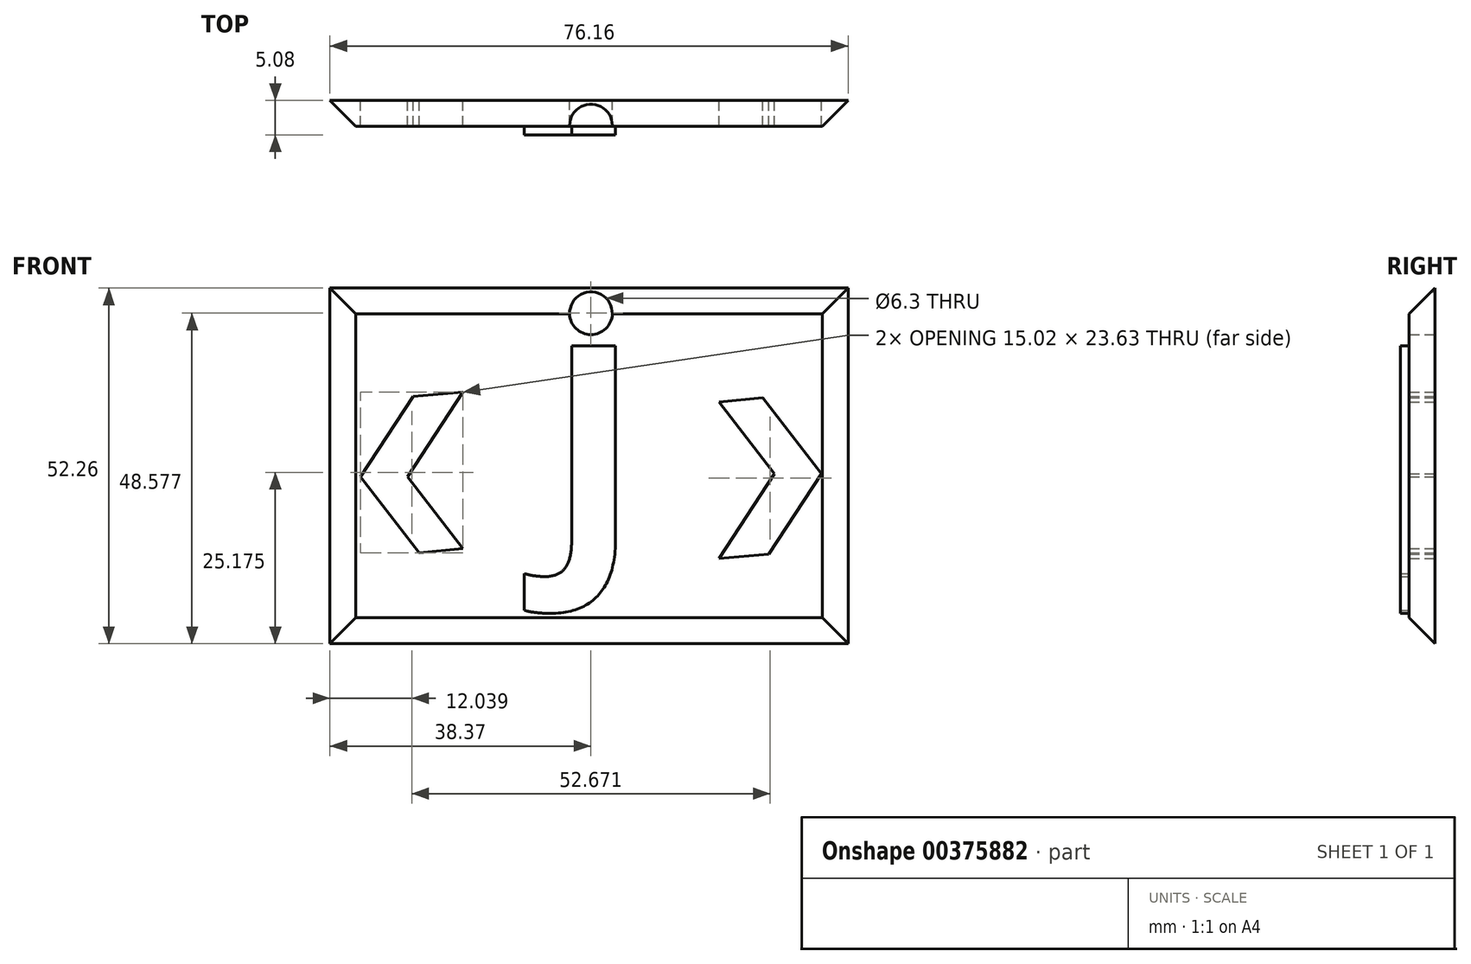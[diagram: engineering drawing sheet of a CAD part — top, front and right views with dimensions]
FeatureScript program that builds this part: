
annotation { "Feature Type Name" : "Feature", "Feature Type Description" : "" }
export const myFeature = defineFeature(function(context is Context, id is Id, definition is map)
    precondition{}
    {
        {
            var Q0;
            Q0=qCreatedBy(makeId("Front.planeOp"),FACE);
            var sketch = newSketch(context, id + "F0", { "sketchPlane" : qUnion([Q0])});
            skPoint(sketch, "E0.cCircle.center.orphan", {"position": v(0, 0) * mm});
            skCircle(sketch, "E1", {"center": v(0, 24.05) * mm, "radius": 3.15 * mm});
            skLineSegment(sketch, "E2", {"start": v(-33.84, 0) * mm, "end": v(-25.23, -11.17) * mm});
            skLineSegment(sketch, "E3", {"start": v(-18.82, 12.46) * mm, "end": v(-26.94, 0) * mm});
            skLineSegment(sketch, "E4", {"start": v(-26.94, 0) * mm, "end": v(-18.82, -10.55) * mm});
            skLineSegment(sketch, "E5", {"start": v(-18.82, -10.55) * mm, "end": v(-25.23, -11.17) * mm});
            skLineSegment(sketch, "E6", {"start": v(-33.84, 0) * mm, "end": v(-26.14, 11.81) * mm});
            skLineSegment(sketch, "E7", {"start": v(-26.14, 11.81) * mm, "end": v(-18.82, 12.46) * mm});
            skText(sketch, "E8", { "text": "J", "fontName": "OpenSans-Bold.ttf"});
            skLineSegment(sketch, "E9", {"start": v(33.85, 0.46) * mm, "end": v(25.24, 11.62) * mm});
            skLineSegment(sketch, "E10", {"start": v(18.83, -12) * mm, "end": v(26.95, 0.46) * mm});
            skLineSegment(sketch, "E11", {"start": v(26.95, 0.46) * mm, "end": v(18.83, 11) * mm});
            skLineSegment(sketch, "E12", {"start": v(18.83, 11) * mm, "end": v(25.24, 11.62) * mm});
            skLineSegment(sketch, "E13", {"start": v(33.85, 0.46) * mm, "end": v(26.15, -11.36) * mm});
            skLineSegment(sketch, "E14", {"start": v(26.15, -11.36) * mm, "end": v(18.83, -12) * mm});
            skLineSegment(sketch, "E15.bottom", {"start": v(39.06, 29) * mm, "end": v(-39.64, 29) * mm});
            skLineSegment(sketch, "E15.top", {"start": v(39.06, -25.8) * mm, "end": v(-39.64, -25.8) * mm});
            skLineSegment(sketch, "E15.left", {"start": v(39.06, 29) * mm, "end": v(39.06, -25.8) * mm});
            skLineSegment(sketch, "E15.right", {"start": v(-39.64, 29) * mm, "end": v(-39.64, -25.8) * mm});
            const initialGuessF0  = {"E8": [-0.00665, -0.01113, 1, 0, 0.03063]};
            skSetInitialGuess(sketch, initialGuessF0);
            skSolve(sketch);
        }
        {
            var Q0;
            Q0=makeQuery(id+"F0.imprint","IMPRINT",FACE,{"disambiguationData":[TD([[makeQuery(id+"F0.imprint","IMPRINT",EDGE,{"derivedFrom":sQuery(id+"F0.wireOp",EDGE,"E1")}),-1.0]])]});
            extrude(context, id + "F1", {"entities" : qUnion([Q0]), "depth" : 3.8 * mm});
        }
        {
            var Q0;
            Q0=makeQuery(id+"F0.imprint","IMPRINT",FACE,{"disambiguationData":[TD([[makeQuery(id+"F0.imprint","IMPRINT",EDGE,{"derivedFrom":sQuery(id+"F0.wireOp",EDGE,"E8.sketch_text.stroke-0")}),-1.0]])]});
            extrude(context, id + "F2", {"entities" : qUnion([Q0]), "operationType" : NewBodyOperationType.ADD, "depth" : 5.08 * mm});
        }
        {
            var Q0;
            Q0=makeQuery(id+"F1.opExtrude","CAP_EDGE",EDGE,{"disambiguationData":[OSD([sQuery(id+"F0.wireOp",EDGE,"E15.right")])],"isStart":false});
            var Q1;
            Q1=makeQuery(id+"F1.opExtrude","CAP_EDGE",EDGE,{"disambiguationData":[OSD([sQuery(id+"F0.wireOp",EDGE,"E15.left")])],"isStart":false});
            var Q2;
            Q2=makeQuery(id+"F1.opExtrude","CAP_EDGE",EDGE,{"disambiguationData":[OSD([sQuery(id+"F0.wireOp",EDGE,"E15.bottom")])],"isStart":false});
            var Q3;
            Q3=makeQuery(id+"F1.opExtrude","CAP_EDGE",EDGE,{"disambiguationData":[OSD([sQuery(id+"F0.wireOp",EDGE,"E15.top")])],"isStart":false});
            chamfer(context, id + "F3", {"entities" : qUnion([Q0, Q1, Q2, Q3]), "width" : 5.08 * mm, "tangentPropagation" : true});
        }
    });
